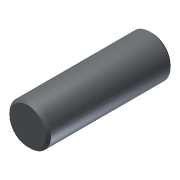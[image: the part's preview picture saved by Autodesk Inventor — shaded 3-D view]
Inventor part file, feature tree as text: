
AUTODESK INVENTOR PART (.ipt)
format: ipt  version: 2013 (Build 170138000, 138)  size: 74,240 bytes
history: native  units: in
note: dims shown in document units (in); Inventor stores cm internally (conversion verified against a paired STEP export)
features: chamfer x1, other x1, imported_body x1
ambient origin geometry x8: Origin, YZ Plane, XZ Plane, XY Plane, X Axis, Y Axis, Z Axis, Center Point
feature tree (3):
  chamfer  "Chamfer1"  [1 undecoded]
  other  "217-2625-010 Rev11"
  imported_body  "Base1"
note: 1 required parameter value undecoded (feature->parameter linkage not recoverable at this tier; creation-order binding heuristic only, values carry confidence <= 0.55)
